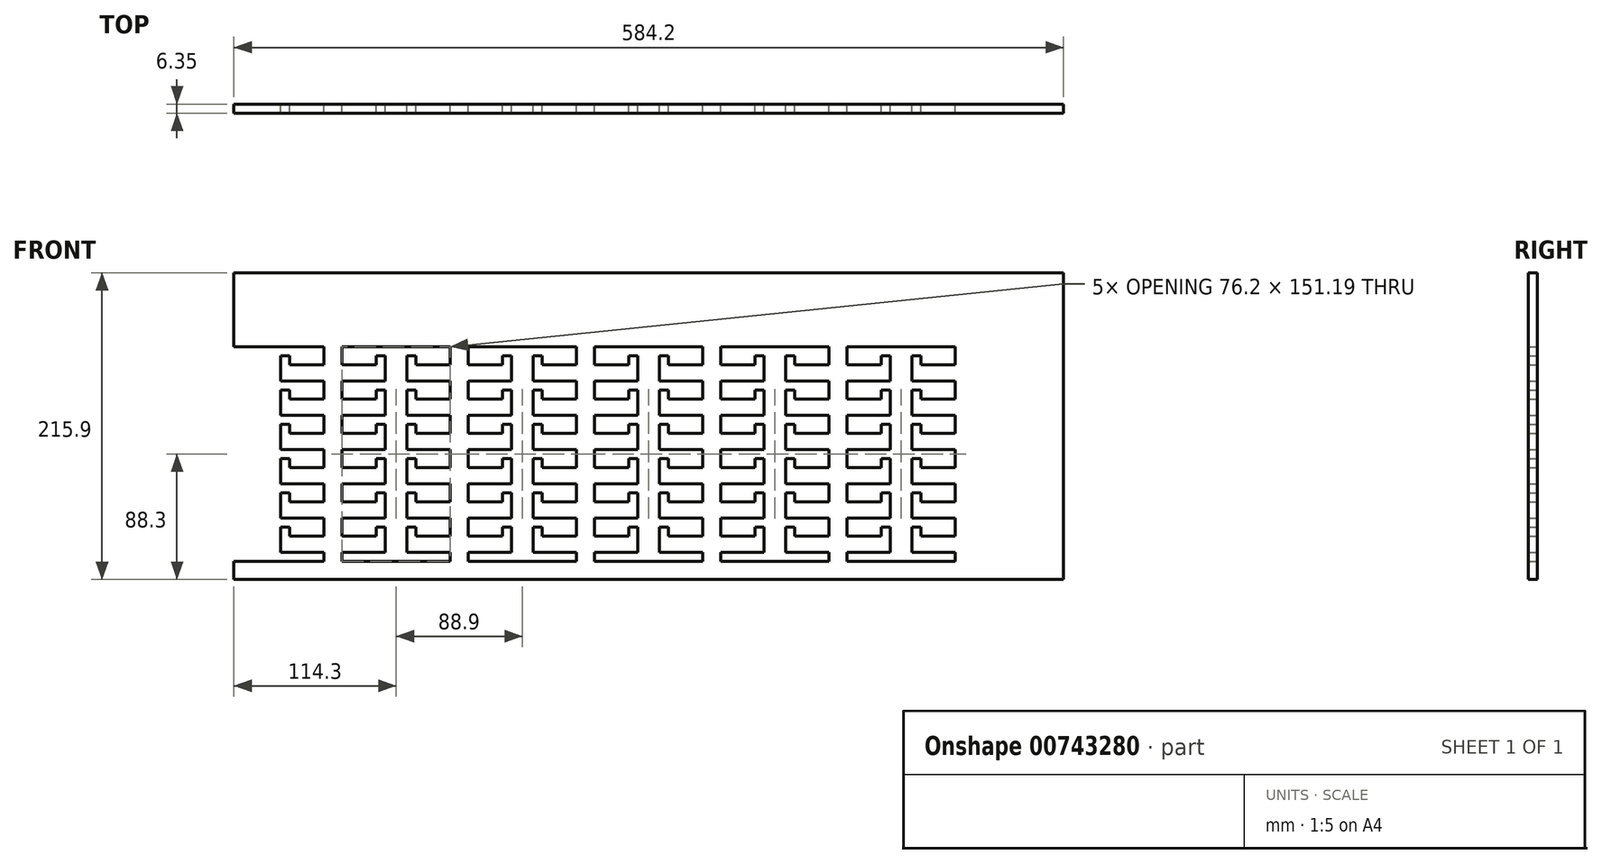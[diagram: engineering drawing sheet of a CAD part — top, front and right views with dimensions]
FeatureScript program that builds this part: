
annotation { "Feature Type Name" : "Feature", "Feature Type Description" : "" }
export const myFeature = defineFeature(function(context is Context, id is Id, definition is map)
    precondition{}
    {
        {
            var Q0;
            Q0=qCreatedBy(makeId("Front.planeOp"),FACE);
            var sketch = newSketch(context, id + "F0", { "sketchPlane" : qUnion([Q0])});
            skLineSegment(sketch, "E0", {"start": v(-97.96, -49.5) * mm, "end": v(-67.48, -49.5) * mm});
            skLineSegment(sketch, "E1", {"start": v(-67.48, -49.5) * mm, "end": v(-67.48, -31.72) * mm});
            skLineSegment(sketch, "E2", {"start": v(-67.48, -31.72) * mm, "end": v(-73.83, -31.72) * mm});
            skLineSegment(sketch, "E3", {"start": v(-73.83, -31.72) * mm, "end": v(-73.83, -38.07) * mm});
            skLineSegment(sketch, "E4", {"start": v(-73.83, -38.07) * mm, "end": v(-97.96, -38.07) * mm});
            skLineSegment(sketch, "E5", {"start": v(-97.96, -38.07) * mm, "end": v(-97.96, -25.37) * mm});
            skLineSegment(sketch, "E6", {"start": v(-97.96, -25.37) * mm, "end": v(-67.48, -25.37) * mm});
            skLineSegment(sketch, "E7", {"start": v(-67.48, -25.37) * mm, "end": v(-67.48, -7.6) * mm});
            skLineSegment(sketch, "E8", {"start": v(-67.48, -7.6) * mm, "end": v(-73.83, -7.6) * mm});
            skLineSegment(sketch, "E9", {"start": v(-73.83, -7.6) * mm, "end": v(-73.83, -13.94) * mm});
            skLineSegment(sketch, "E10", {"start": v(-73.83, -13.94) * mm, "end": v(-97.96, -13.94) * mm});
            skLineSegment(sketch, "E11", {"start": v(-97.96, -13.94) * mm, "end": v(-97.96, -1.24) * mm});
            skLineSegment(sketch, "E12", {"start": v(-97.96, -1.24) * mm, "end": v(-67.48, -1.24) * mm});
            skLineSegment(sketch, "E13", {"start": v(-67.48, -1.24) * mm, "end": v(-67.48, 16.54) * mm});
            skLineSegment(sketch, "E14", {"start": v(-67.48, 16.54) * mm, "end": v(-73.83, 16.54) * mm});
            skLineSegment(sketch, "E15", {"start": v(-73.83, 16.54) * mm, "end": v(-73.83, 10.19) * mm});
            skLineSegment(sketch, "E16", {"start": v(-73.83, 10.19) * mm, "end": v(-97.96, 10.19) * mm});
            skLineSegment(sketch, "E17", {"start": v(-97.96, 10.19) * mm, "end": v(-97.96, 22.89) * mm});
            skLineSegment(sketch, "E18", {"start": v(-97.96, 22.89) * mm, "end": v(-67.48, 22.89) * mm});
            skLineSegment(sketch, "E19", {"start": v(-67.48, 22.89) * mm, "end": v(-67.48, 40.67) * mm});
            skLineSegment(sketch, "E20", {"start": v(-67.48, 40.67) * mm, "end": v(-73.83, 40.67) * mm});
            skLineSegment(sketch, "E21", {"start": v(-73.83, 40.67) * mm, "end": v(-73.83, 34.32) * mm});
            skLineSegment(sketch, "E22", {"start": v(-73.83, 34.32) * mm, "end": v(-97.96, 34.32) * mm});
            skLineSegment(sketch, "E23", {"start": v(-97.96, 34.32) * mm, "end": v(-97.96, 47.02) * mm});
            skLineSegment(sketch, "E24", {"start": v(-97.96, 47.02) * mm, "end": v(-67.48, 47.02) * mm});
            skLineSegment(sketch, "E25", {"start": v(-67.48, 64.8) * mm, "end": v(-73.83, 64.8) * mm});
            skLineSegment(sketch, "E26", {"start": v(-73.83, 64.8) * mm, "end": v(-73.83, 58.45) * mm});
            skLineSegment(sketch, "E27", {"start": v(-73.83, 58.45) * mm, "end": v(-97.96, 58.45) * mm});
            skLineSegment(sketch, "E28", {"start": v(-97.96, 58.45) * mm, "end": v(-97.96, 71.15) * mm});
            skLineSegment(sketch, "E29", {"start": v(-21.76, -80.05) * mm, "end": v(-21.76, -73.63) * mm});
            skLineSegment(sketch, "E30", {"start": v(-21.76, -73.63) * mm, "end": v(-52.24, -73.63) * mm});
            skLineSegment(sketch, "E31", {"start": v(-52.24, -73.63) * mm, "end": v(-52.24, -55.85) * mm});
            skLineSegment(sketch, "E32", {"start": v(-52.24, -55.85) * mm, "end": v(-45.89, -55.85) * mm});
            skLineSegment(sketch, "E33", {"start": v(-45.89, -55.85) * mm, "end": v(-45.89, -62.2) * mm});
            skLineSegment(sketch, "E34", {"start": v(-45.89, -62.2) * mm, "end": v(-21.76, -62.2) * mm});
            skLineSegment(sketch, "E35", {"start": v(-21.76, -62.2) * mm, "end": v(-21.76, -49.5) * mm});
            skLineSegment(sketch, "E36", {"start": v(-21.76, -49.5) * mm, "end": v(-52.24, -49.5) * mm});
            skLineSegment(sketch, "E37", {"start": v(-52.24, -49.5) * mm, "end": v(-52.24, -31.72) * mm});
            skLineSegment(sketch, "E38", {"start": v(-52.24, -31.72) * mm, "end": v(-45.89, -31.72) * mm});
            skLineSegment(sketch, "E39", {"start": v(-45.89, -31.72) * mm, "end": v(-45.89, -38.07) * mm});
            skLineSegment(sketch, "E40", {"start": v(-45.89, -38.07) * mm, "end": v(-21.76, -38.07) * mm});
            skLineSegment(sketch, "E41", {"start": v(-21.76, -38.07) * mm, "end": v(-21.76, -25.37) * mm});
            skLineSegment(sketch, "E42", {"start": v(-21.76, -25.37) * mm, "end": v(-52.24, -25.37) * mm});
            skLineSegment(sketch, "E43", {"start": v(-52.24, -25.37) * mm, "end": v(-52.24, -7.6) * mm});
            skLineSegment(sketch, "E44", {"start": v(-52.24, -7.6) * mm, "end": v(-45.89, -7.6) * mm});
            skLineSegment(sketch, "E45", {"start": v(-45.89, -7.6) * mm, "end": v(-45.89, -13.94) * mm});
            skLineSegment(sketch, "E46", {"start": v(-45.89, -13.94) * mm, "end": v(-21.76, -13.94) * mm});
            skLineSegment(sketch, "E47", {"start": v(-21.76, -13.94) * mm, "end": v(-21.76, -1.24) * mm});
            skLineSegment(sketch, "E48", {"start": v(-21.76, -1.24) * mm, "end": v(-52.24, -1.24) * mm});
            skLineSegment(sketch, "E49", {"start": v(-52.24, -1.24) * mm, "end": v(-52.24, 16.54) * mm});
            skLineSegment(sketch, "E50", {"start": v(-52.24, 16.54) * mm, "end": v(-45.89, 16.54) * mm});
            skLineSegment(sketch, "E51", {"start": v(-45.89, 16.54) * mm, "end": v(-45.89, 10.19) * mm});
            skLineSegment(sketch, "E52", {"start": v(-45.89, 10.19) * mm, "end": v(-21.76, 10.19) * mm});
            skLineSegment(sketch, "E53", {"start": v(-21.76, 10.19) * mm, "end": v(-21.76, 22.89) * mm});
            skLineSegment(sketch, "E54", {"start": v(-21.76, 22.89) * mm, "end": v(-52.24, 22.89) * mm});
            skLineSegment(sketch, "E55", {"start": v(-52.24, 22.89) * mm, "end": v(-52.24, 40.67) * mm});
            skLineSegment(sketch, "E56", {"start": v(-52.24, 40.67) * mm, "end": v(-45.89, 40.67) * mm});
            skLineSegment(sketch, "E57", {"start": v(-45.89, 40.67) * mm, "end": v(-45.89, 34.32) * mm});
            skLineSegment(sketch, "E58", {"start": v(-45.89, 34.32) * mm, "end": v(-21.76, 34.32) * mm});
            skLineSegment(sketch, "E59", {"start": v(-21.76, 34.32) * mm, "end": v(-21.76, 47.02) * mm});
            skLineSegment(sketch, "E60", {"start": v(-21.76, 47.02) * mm, "end": v(-52.24, 47.02) * mm});
            skLineSegment(sketch, "E61", {"start": v(-52.24, 47.02) * mm, "end": v(-52.24, 64.8) * mm});
            skLineSegment(sketch, "E62", {"start": v(-52.24, 64.8) * mm, "end": v(-45.89, 64.8) * mm});
            skLineSegment(sketch, "E63", {"start": v(-45.89, 64.8) * mm, "end": v(-45.89, 58.45) * mm});
            skLineSegment(sketch, "E64", {"start": v(-45.89, 58.45) * mm, "end": v(-21.76, 58.45) * mm});
            skLineSegment(sketch, "E65", {"start": v(-21.76, 58.45) * mm, "end": v(-21.76, 71.15) * mm});
            skLineSegment(sketch, "E66", {"start": v(-67.48, 47.02) * mm, "end": v(-67.48, 64.8) * mm});
            skLineSegment(sketch, "E67", {"start": v(-67.48, -73.63) * mm, "end": v(-67.48, -55.85) * mm});
            skLineSegment(sketch, "E68", {"start": v(-73.83, -62.2) * mm, "end": v(-73.83, -55.85) * mm});
            skLineSegment(sketch, "E69", {"start": v(-73.83, -55.85) * mm, "end": v(-67.48, -55.85) * mm});
            skLineSegment(sketch, "E70", {"start": v(-67.48, -73.63) * mm, "end": v(-97.96, -73.63) * mm});
            skLineSegment(sketch, "E71", {"start": v(-97.96, -62.2) * mm, "end": v(-97.96, -49.5) * mm});
            skLineSegment(sketch, "E72", {"start": v(-97.96, -73.63) * mm, "end": v(-97.96, -80.05) * mm});
            skLineSegment(sketch, "E73", {"start": v(-97.96, -62.2) * mm, "end": v(-73.83, -62.2) * mm});
            skLineSegment(sketch, "E74", {"start": v(-97.96, -80.05) * mm, "end": v(-21.76, -80.05) * mm});
            skLineSegment(sketch, "E75", {"start": v(-97.96, 71.15) * mm, "end": v(-21.76, 71.15) * mm});
            skPoint(sketch, "E76", {"position": v(-59.86, 71.15) * mm});
            skPoint(sketch, "E77", {"position": v(-59.86, -80.05) * mm});
            skLineSegment(sketch, "E78", {"start": v(-186.86, -49.5) * mm, "end": v(-156.38, -49.5) * mm});
            skLineSegment(sketch, "E79", {"start": v(-156.38, -49.5) * mm, "end": v(-156.38, -31.72) * mm});
            skLineSegment(sketch, "E80", {"start": v(-156.38, -31.72) * mm, "end": v(-162.73, -31.72) * mm});
            skLineSegment(sketch, "E81", {"start": v(-162.73, -31.72) * mm, "end": v(-162.73, -38.07) * mm});
            skLineSegment(sketch, "E82", {"start": v(-162.73, -38.07) * mm, "end": v(-186.86, -38.07) * mm});
            skLineSegment(sketch, "E83", {"start": v(-186.86, -38.07) * mm, "end": v(-186.86, -25.37) * mm});
            skLineSegment(sketch, "E84", {"start": v(-186.86, -25.37) * mm, "end": v(-156.38, -25.37) * mm});
            skLineSegment(sketch, "E85", {"start": v(-156.38, -25.37) * mm, "end": v(-156.38, -7.6) * mm});
            skLineSegment(sketch, "E86", {"start": v(-156.38, -7.6) * mm, "end": v(-162.73, -7.6) * mm});
            skLineSegment(sketch, "E87", {"start": v(-162.73, -7.6) * mm, "end": v(-162.73, -13.94) * mm});
            skLineSegment(sketch, "E88", {"start": v(-162.73, -13.94) * mm, "end": v(-186.86, -13.94) * mm});
            skLineSegment(sketch, "E89", {"start": v(-186.86, -13.94) * mm, "end": v(-186.86, -1.24) * mm});
            skLineSegment(sketch, "E90", {"start": v(-186.86, -1.24) * mm, "end": v(-156.38, -1.24) * mm});
            skLineSegment(sketch, "E91", {"start": v(-156.38, -1.24) * mm, "end": v(-156.38, 16.54) * mm});
            skLineSegment(sketch, "E92", {"start": v(-156.38, 16.54) * mm, "end": v(-162.73, 16.54) * mm});
            skLineSegment(sketch, "E93", {"start": v(-162.73, 16.54) * mm, "end": v(-162.73, 10.19) * mm});
            skLineSegment(sketch, "E94", {"start": v(-162.73, 10.19) * mm, "end": v(-186.86, 10.19) * mm});
            skLineSegment(sketch, "E95", {"start": v(-186.86, 10.19) * mm, "end": v(-186.86, 22.89) * mm});
            skLineSegment(sketch, "E96", {"start": v(-186.86, 22.89) * mm, "end": v(-156.38, 22.89) * mm});
            skLineSegment(sketch, "E97", {"start": v(-156.38, 22.89) * mm, "end": v(-156.38, 40.67) * mm});
            skLineSegment(sketch, "E98", {"start": v(-156.38, 40.67) * mm, "end": v(-162.73, 40.67) * mm});
            skLineSegment(sketch, "E99", {"start": v(-162.73, 40.67) * mm, "end": v(-162.73, 34.32) * mm});
            skLineSegment(sketch, "E100", {"start": v(-162.73, 34.32) * mm, "end": v(-186.86, 34.32) * mm});
            skLineSegment(sketch, "E101", {"start": v(-186.86, 34.32) * mm, "end": v(-186.86, 47.02) * mm});
            skLineSegment(sketch, "E102", {"start": v(-186.86, 47.02) * mm, "end": v(-156.38, 47.02) * mm});
            skLineSegment(sketch, "E103", {"start": v(-156.38, 64.8) * mm, "end": v(-162.73, 64.8) * mm});
            skLineSegment(sketch, "E104", {"start": v(-162.73, 64.8) * mm, "end": v(-162.73, 58.45) * mm});
            skLineSegment(sketch, "E105", {"start": v(-162.73, 58.45) * mm, "end": v(-186.86, 58.45) * mm});
            skLineSegment(sketch, "E106", {"start": v(-186.86, 58.45) * mm, "end": v(-186.86, 71.15) * mm});
            skLineSegment(sketch, "E107", {"start": v(-110.66, -80.05) * mm, "end": v(-110.66, -73.63) * mm});
            skLineSegment(sketch, "E108", {"start": v(-110.66, -73.63) * mm, "end": v(-141.14, -73.63) * mm});
            skLineSegment(sketch, "E109", {"start": v(-141.14, -73.63) * mm, "end": v(-141.14, -55.85) * mm});
            skLineSegment(sketch, "E110", {"start": v(-141.14, -55.85) * mm, "end": v(-134.79, -55.85) * mm});
            skLineSegment(sketch, "E111", {"start": v(-134.79, -55.85) * mm, "end": v(-134.79, -62.2) * mm});
            skLineSegment(sketch, "E112", {"start": v(-134.79, -62.2) * mm, "end": v(-110.66, -62.2) * mm});
            skLineSegment(sketch, "E113", {"start": v(-110.66, -62.2) * mm, "end": v(-110.66, -49.5) * mm});
            skLineSegment(sketch, "E114", {"start": v(-110.66, -49.5) * mm, "end": v(-141.14, -49.5) * mm});
            skLineSegment(sketch, "E115", {"start": v(-141.14, -49.5) * mm, "end": v(-141.14, -31.72) * mm});
            skLineSegment(sketch, "E116", {"start": v(-141.14, -31.72) * mm, "end": v(-134.79, -31.72) * mm});
            skLineSegment(sketch, "E117", {"start": v(-134.79, -31.72) * mm, "end": v(-134.79, -38.07) * mm});
            skLineSegment(sketch, "E118", {"start": v(-134.79, -38.07) * mm, "end": v(-110.66, -38.07) * mm});
            skLineSegment(sketch, "E119", {"start": v(-110.66, -38.07) * mm, "end": v(-110.66, -25.37) * mm});
            skLineSegment(sketch, "E120", {"start": v(-110.66, -25.37) * mm, "end": v(-141.14, -25.37) * mm});
            skLineSegment(sketch, "E121", {"start": v(-141.14, -25.37) * mm, "end": v(-141.14, -7.6) * mm});
            skLineSegment(sketch, "E122", {"start": v(-141.14, -7.6) * mm, "end": v(-134.79, -7.6) * mm});
            skLineSegment(sketch, "E123", {"start": v(-134.79, -7.6) * mm, "end": v(-134.79, -13.94) * mm});
            skLineSegment(sketch, "E124", {"start": v(-134.79, -13.94) * mm, "end": v(-110.66, -13.94) * mm});
            skLineSegment(sketch, "E125", {"start": v(-110.66, -13.94) * mm, "end": v(-110.66, -1.24) * mm});
            skLineSegment(sketch, "E126", {"start": v(-110.66, -1.24) * mm, "end": v(-141.14, -1.24) * mm});
            skLineSegment(sketch, "E127", {"start": v(-141.14, -1.24) * mm, "end": v(-141.14, 16.54) * mm});
            skLineSegment(sketch, "E128", {"start": v(-141.14, 16.54) * mm, "end": v(-134.79, 16.54) * mm});
            skLineSegment(sketch, "E129", {"start": v(-134.79, 16.54) * mm, "end": v(-134.79, 10.19) * mm});
            skLineSegment(sketch, "E130", {"start": v(-134.79, 10.19) * mm, "end": v(-110.66, 10.19) * mm});
            skLineSegment(sketch, "E131", {"start": v(-110.66, 10.19) * mm, "end": v(-110.66, 22.89) * mm});
            skLineSegment(sketch, "E132", {"start": v(-110.66, 22.89) * mm, "end": v(-141.14, 22.89) * mm});
            skLineSegment(sketch, "E133", {"start": v(-141.14, 22.89) * mm, "end": v(-141.14, 40.67) * mm});
            skLineSegment(sketch, "E134", {"start": v(-141.14, 40.67) * mm, "end": v(-134.79, 40.67) * mm});
            skLineSegment(sketch, "E135", {"start": v(-134.79, 40.67) * mm, "end": v(-134.79, 34.32) * mm});
            skLineSegment(sketch, "E136", {"start": v(-134.79, 34.32) * mm, "end": v(-110.66, 34.32) * mm});
            skLineSegment(sketch, "E137", {"start": v(-110.66, 34.32) * mm, "end": v(-110.66, 47.02) * mm});
            skLineSegment(sketch, "E138", {"start": v(-110.66, 47.02) * mm, "end": v(-141.14, 47.02) * mm});
            skLineSegment(sketch, "E139", {"start": v(-141.14, 47.02) * mm, "end": v(-141.14, 64.8) * mm});
            skLineSegment(sketch, "E140", {"start": v(-141.14, 64.8) * mm, "end": v(-134.79, 64.8) * mm});
            skLineSegment(sketch, "E141", {"start": v(-134.79, 64.8) * mm, "end": v(-134.79, 58.45) * mm});
            skLineSegment(sketch, "E142", {"start": v(-134.79, 58.45) * mm, "end": v(-110.66, 58.45) * mm});
            skLineSegment(sketch, "E143", {"start": v(-110.66, 58.45) * mm, "end": v(-110.66, 71.15) * mm});
            skLineSegment(sketch, "E144", {"start": v(-156.38, 47.02) * mm, "end": v(-156.38, 64.8) * mm});
            skLineSegment(sketch, "E145", {"start": v(-156.38, -73.63) * mm, "end": v(-156.38, -55.85) * mm});
            skLineSegment(sketch, "E146", {"start": v(-162.73, -62.2) * mm, "end": v(-162.73, -55.85) * mm});
            skLineSegment(sketch, "E147", {"start": v(-162.73, -55.85) * mm, "end": v(-156.38, -55.85) * mm});
            skLineSegment(sketch, "E148", {"start": v(-156.38, -73.63) * mm, "end": v(-186.86, -73.63) * mm});
            skLineSegment(sketch, "E149", {"start": v(-186.86, -62.2) * mm, "end": v(-186.86, -49.5) * mm});
            skLineSegment(sketch, "E150", {"start": v(-186.86, -73.63) * mm, "end": v(-186.86, -80.05) * mm});
            skLineSegment(sketch, "E151", {"start": v(-186.86, -62.2) * mm, "end": v(-162.73, -62.2) * mm});
            skLineSegment(sketch, "E152", {"start": v(-186.86, -80.05) * mm, "end": v(-110.66, -80.05) * mm});
            skLineSegment(sketch, "E153", {"start": v(-186.86, 71.15) * mm, "end": v(-110.66, 71.15) * mm});
            skPoint(sketch, "E154", {"position": v(-148.76, 71.15) * mm});
            skPoint(sketch, "E155", {"position": v(-148.76, -80.05) * mm});
            skLineSegment(sketch, "E156", {"start": v(-275.76, -49.5) * mm, "end": v(-245.28, -49.5) * mm});
            skLineSegment(sketch, "E157", {"start": v(-245.28, -49.5) * mm, "end": v(-245.28, -31.72) * mm});
            skLineSegment(sketch, "E158", {"start": v(-245.28, -31.72) * mm, "end": v(-251.63, -31.72) * mm});
            skLineSegment(sketch, "E159", {"start": v(-251.63, -31.72) * mm, "end": v(-251.63, -38.07) * mm});
            skLineSegment(sketch, "E160", {"start": v(-251.63, -38.07) * mm, "end": v(-275.76, -38.07) * mm});
            skLineSegment(sketch, "E161", {"start": v(-275.76, -38.07) * mm, "end": v(-275.76, -25.37) * mm});
            skLineSegment(sketch, "E162", {"start": v(-275.76, -25.37) * mm, "end": v(-245.28, -25.37) * mm});
            skLineSegment(sketch, "E163", {"start": v(-245.28, -25.37) * mm, "end": v(-245.28, -7.6) * mm});
            skLineSegment(sketch, "E164", {"start": v(-245.28, -7.6) * mm, "end": v(-251.63, -7.6) * mm});
            skLineSegment(sketch, "E165", {"start": v(-251.63, -7.6) * mm, "end": v(-251.63, -13.94) * mm});
            skLineSegment(sketch, "E166", {"start": v(-251.63, -13.94) * mm, "end": v(-275.76, -13.94) * mm});
            skLineSegment(sketch, "E167", {"start": v(-275.76, -13.94) * mm, "end": v(-275.76, -1.24) * mm});
            skLineSegment(sketch, "E168", {"start": v(-275.76, -1.24) * mm, "end": v(-245.28, -1.24) * mm});
            skLineSegment(sketch, "E169", {"start": v(-245.28, -1.24) * mm, "end": v(-245.28, 16.54) * mm});
            skLineSegment(sketch, "E170", {"start": v(-245.28, 16.54) * mm, "end": v(-251.63, 16.54) * mm});
            skLineSegment(sketch, "E171", {"start": v(-251.63, 16.54) * mm, "end": v(-251.63, 10.19) * mm});
            skLineSegment(sketch, "E172", {"start": v(-251.63, 10.19) * mm, "end": v(-275.76, 10.19) * mm});
            skLineSegment(sketch, "E173", {"start": v(-275.76, 10.19) * mm, "end": v(-275.76, 22.89) * mm});
            skLineSegment(sketch, "E174", {"start": v(-275.76, 22.89) * mm, "end": v(-245.28, 22.89) * mm});
            skLineSegment(sketch, "E175", {"start": v(-245.28, 22.89) * mm, "end": v(-245.28, 40.67) * mm});
            skLineSegment(sketch, "E176", {"start": v(-245.28, 40.67) * mm, "end": v(-251.63, 40.67) * mm});
            skLineSegment(sketch, "E177", {"start": v(-251.63, 40.67) * mm, "end": v(-251.63, 34.32) * mm});
            skLineSegment(sketch, "E178", {"start": v(-251.63, 34.32) * mm, "end": v(-275.76, 34.32) * mm});
            skLineSegment(sketch, "E179", {"start": v(-275.76, 34.32) * mm, "end": v(-275.76, 47.02) * mm});
            skLineSegment(sketch, "E180", {"start": v(-275.76, 47.02) * mm, "end": v(-245.28, 47.02) * mm});
            skLineSegment(sketch, "E181", {"start": v(-245.28, 64.8) * mm, "end": v(-251.63, 64.8) * mm});
            skLineSegment(sketch, "E182", {"start": v(-251.63, 64.8) * mm, "end": v(-251.63, 58.45) * mm});
            skLineSegment(sketch, "E183", {"start": v(-251.63, 58.45) * mm, "end": v(-275.76, 58.45) * mm});
            skLineSegment(sketch, "E184", {"start": v(-275.76, 58.45) * mm, "end": v(-275.76, 71.15) * mm});
            skLineSegment(sketch, "E185", {"start": v(-199.56, -80.05) * mm, "end": v(-199.56, -73.63) * mm});
            skLineSegment(sketch, "E186", {"start": v(-199.56, -73.63) * mm, "end": v(-230.04, -73.63) * mm});
            skLineSegment(sketch, "E187", {"start": v(-230.04, -73.63) * mm, "end": v(-230.04, -55.85) * mm});
            skLineSegment(sketch, "E188", {"start": v(-230.04, -55.85) * mm, "end": v(-223.69, -55.85) * mm});
            skLineSegment(sketch, "E189", {"start": v(-223.69, -55.85) * mm, "end": v(-223.69, -62.2) * mm});
            skLineSegment(sketch, "E190", {"start": v(-223.69, -62.2) * mm, "end": v(-199.56, -62.2) * mm});
            skLineSegment(sketch, "E191", {"start": v(-199.56, -62.2) * mm, "end": v(-199.56, -49.5) * mm});
            skLineSegment(sketch, "E192", {"start": v(-199.56, -49.5) * mm, "end": v(-230.04, -49.5) * mm});
            skLineSegment(sketch, "E193", {"start": v(-230.04, -49.5) * mm, "end": v(-230.04, -31.72) * mm});
            skLineSegment(sketch, "E194", {"start": v(-230.04, -31.72) * mm, "end": v(-223.69, -31.72) * mm});
            skLineSegment(sketch, "E195", {"start": v(-223.69, -31.72) * mm, "end": v(-223.69, -38.07) * mm});
            skLineSegment(sketch, "E196", {"start": v(-223.69, -38.07) * mm, "end": v(-199.56, -38.07) * mm});
            skLineSegment(sketch, "E197", {"start": v(-199.56, -38.07) * mm, "end": v(-199.56, -25.37) * mm});
            skLineSegment(sketch, "E198", {"start": v(-199.56, -25.37) * mm, "end": v(-230.04, -25.37) * mm});
            skLineSegment(sketch, "E199", {"start": v(-230.04, -25.37) * mm, "end": v(-230.04, -7.6) * mm});
            skLineSegment(sketch, "E200", {"start": v(-230.04, -7.6) * mm, "end": v(-223.69, -7.6) * mm});
            skLineSegment(sketch, "E201", {"start": v(-223.69, -7.6) * mm, "end": v(-223.69, -13.94) * mm});
            skLineSegment(sketch, "E202", {"start": v(-223.69, -13.94) * mm, "end": v(-199.56, -13.94) * mm});
            skLineSegment(sketch, "E203", {"start": v(-199.56, -13.94) * mm, "end": v(-199.56, -1.24) * mm});
            skLineSegment(sketch, "E204", {"start": v(-199.56, -1.24) * mm, "end": v(-230.04, -1.24) * mm});
            skLineSegment(sketch, "E205", {"start": v(-230.04, -1.24) * mm, "end": v(-230.04, 16.54) * mm});
            skLineSegment(sketch, "E206", {"start": v(-230.04, 16.54) * mm, "end": v(-223.69, 16.54) * mm});
            skLineSegment(sketch, "E207", {"start": v(-223.69, 16.54) * mm, "end": v(-223.69, 10.19) * mm});
            skLineSegment(sketch, "E208", {"start": v(-223.69, 10.19) * mm, "end": v(-199.56, 10.19) * mm});
            skLineSegment(sketch, "E209", {"start": v(-199.56, 10.19) * mm, "end": v(-199.56, 22.89) * mm});
            skLineSegment(sketch, "E210", {"start": v(-199.56, 22.89) * mm, "end": v(-230.04, 22.89) * mm});
            skLineSegment(sketch, "E211", {"start": v(-230.04, 22.89) * mm, "end": v(-230.04, 40.67) * mm});
            skLineSegment(sketch, "E212", {"start": v(-230.04, 40.67) * mm, "end": v(-223.69, 40.67) * mm});
            skLineSegment(sketch, "E213", {"start": v(-223.69, 40.67) * mm, "end": v(-223.69, 34.32) * mm});
            skLineSegment(sketch, "E214", {"start": v(-223.69, 34.32) * mm, "end": v(-199.56, 34.32) * mm});
            skLineSegment(sketch, "E215", {"start": v(-199.56, 34.32) * mm, "end": v(-199.56, 47.02) * mm});
            skLineSegment(sketch, "E216", {"start": v(-199.56, 47.02) * mm, "end": v(-230.04, 47.02) * mm});
            skLineSegment(sketch, "E217", {"start": v(-230.04, 47.02) * mm, "end": v(-230.04, 64.8) * mm});
            skLineSegment(sketch, "E218", {"start": v(-230.04, 64.8) * mm, "end": v(-223.69, 64.8) * mm});
            skLineSegment(sketch, "E219", {"start": v(-223.69, 64.8) * mm, "end": v(-223.69, 58.45) * mm});
            skLineSegment(sketch, "E220", {"start": v(-223.69, 58.45) * mm, "end": v(-199.56, 58.45) * mm});
            skLineSegment(sketch, "E221", {"start": v(-199.56, 58.45) * mm, "end": v(-199.56, 71.15) * mm});
            skLineSegment(sketch, "E222", {"start": v(-245.28, 47.02) * mm, "end": v(-245.28, 64.8) * mm});
            skLineSegment(sketch, "E223", {"start": v(-245.28, -73.63) * mm, "end": v(-245.28, -55.85) * mm});
            skLineSegment(sketch, "E224", {"start": v(-251.63, -62.2) * mm, "end": v(-251.63, -55.85) * mm});
            skLineSegment(sketch, "E225", {"start": v(-251.63, -55.85) * mm, "end": v(-245.28, -55.85) * mm});
            skLineSegment(sketch, "E226", {"start": v(-245.28, -73.63) * mm, "end": v(-275.76, -73.63) * mm});
            skLineSegment(sketch, "E227", {"start": v(-275.76, -62.2) * mm, "end": v(-275.76, -49.5) * mm});
            skLineSegment(sketch, "E228", {"start": v(-275.76, -73.63) * mm, "end": v(-275.76, -80.05) * mm});
            skLineSegment(sketch, "E229", {"start": v(-275.76, -62.2) * mm, "end": v(-251.63, -62.2) * mm});
            skLineSegment(sketch, "E230", {"start": v(-275.76, -80.05) * mm, "end": v(-199.56, -80.05) * mm});
            skLineSegment(sketch, "E231", {"start": v(-275.76, 71.15) * mm, "end": v(-199.56, 71.15) * mm});
            skPoint(sketch, "E232", {"position": v(-237.66, 71.15) * mm});
            skPoint(sketch, "E233", {"position": v(-237.66, -80.05) * mm});
            skLineSegment(sketch, "E234", {"start": v(-364.66, -49.5) * mm, "end": v(-334.18, -49.5) * mm});
            skLineSegment(sketch, "E235", {"start": v(-334.18, -49.5) * mm, "end": v(-334.18, -31.72) * mm});
            skLineSegment(sketch, "E236", {"start": v(-334.18, -31.72) * mm, "end": v(-340.53, -31.72) * mm});
            skLineSegment(sketch, "E237", {"start": v(-340.53, -31.72) * mm, "end": v(-340.53, -38.07) * mm});
            skLineSegment(sketch, "E238", {"start": v(-340.53, -38.07) * mm, "end": v(-364.66, -38.07) * mm});
            skLineSegment(sketch, "E239", {"start": v(-364.66, -38.07) * mm, "end": v(-364.66, -25.37) * mm});
            skLineSegment(sketch, "E240", {"start": v(-364.66, -25.37) * mm, "end": v(-334.18, -25.37) * mm});
            skLineSegment(sketch, "E241", {"start": v(-334.18, -25.37) * mm, "end": v(-334.18, -7.6) * mm});
            skLineSegment(sketch, "E242", {"start": v(-334.18, -7.6) * mm, "end": v(-340.53, -7.6) * mm});
            skLineSegment(sketch, "E243", {"start": v(-340.53, -7.6) * mm, "end": v(-340.53, -13.94) * mm});
            skLineSegment(sketch, "E244", {"start": v(-340.53, -13.94) * mm, "end": v(-364.66, -13.94) * mm});
            skLineSegment(sketch, "E245", {"start": v(-364.66, -13.94) * mm, "end": v(-364.66, -1.24) * mm});
            skLineSegment(sketch, "E246", {"start": v(-364.66, -1.24) * mm, "end": v(-334.18, -1.24) * mm});
            skLineSegment(sketch, "E247", {"start": v(-334.18, -1.24) * mm, "end": v(-334.18, 16.54) * mm});
            skLineSegment(sketch, "E248", {"start": v(-334.18, 16.54) * mm, "end": v(-340.53, 16.54) * mm});
            skLineSegment(sketch, "E249", {"start": v(-340.53, 16.54) * mm, "end": v(-340.53, 10.19) * mm});
            skLineSegment(sketch, "E250", {"start": v(-340.53, 10.19) * mm, "end": v(-364.66, 10.19) * mm});
            skLineSegment(sketch, "E251", {"start": v(-364.66, 10.19) * mm, "end": v(-364.66, 22.89) * mm});
            skLineSegment(sketch, "E252", {"start": v(-364.66, 22.89) * mm, "end": v(-334.18, 22.89) * mm});
            skLineSegment(sketch, "E253", {"start": v(-334.18, 22.89) * mm, "end": v(-334.18, 40.67) * mm});
            skLineSegment(sketch, "E254", {"start": v(-334.18, 40.67) * mm, "end": v(-340.53, 40.67) * mm});
            skLineSegment(sketch, "E255", {"start": v(-340.53, 40.67) * mm, "end": v(-340.53, 34.32) * mm});
            skLineSegment(sketch, "E256", {"start": v(-340.53, 34.32) * mm, "end": v(-364.66, 34.32) * mm});
            skLineSegment(sketch, "E257", {"start": v(-364.66, 34.32) * mm, "end": v(-364.66, 47.02) * mm});
            skLineSegment(sketch, "E258", {"start": v(-364.66, 47.02) * mm, "end": v(-334.18, 47.02) * mm});
            skLineSegment(sketch, "E259", {"start": v(-334.18, 64.8) * mm, "end": v(-340.53, 64.8) * mm});
            skLineSegment(sketch, "E260", {"start": v(-340.53, 64.8) * mm, "end": v(-340.53, 58.45) * mm});
            skLineSegment(sketch, "E261", {"start": v(-340.53, 58.45) * mm, "end": v(-364.66, 58.45) * mm});
            skLineSegment(sketch, "E262", {"start": v(-364.66, 58.45) * mm, "end": v(-364.66, 71.15) * mm});
            skLineSegment(sketch, "E263", {"start": v(-288.46, -80.05) * mm, "end": v(-288.46, -73.63) * mm});
            skLineSegment(sketch, "E264", {"start": v(-288.46, -73.63) * mm, "end": v(-318.94, -73.63) * mm});
            skLineSegment(sketch, "E265", {"start": v(-318.94, -73.63) * mm, "end": v(-318.94, -55.85) * mm});
            skLineSegment(sketch, "E266", {"start": v(-318.94, -55.85) * mm, "end": v(-312.59, -55.85) * mm});
            skLineSegment(sketch, "E267", {"start": v(-312.59, -55.85) * mm, "end": v(-312.59, -62.2) * mm});
            skLineSegment(sketch, "E268", {"start": v(-312.59, -62.2) * mm, "end": v(-288.46, -62.2) * mm});
            skLineSegment(sketch, "E269", {"start": v(-288.46, -62.2) * mm, "end": v(-288.46, -49.5) * mm});
            skLineSegment(sketch, "E270", {"start": v(-288.46, -49.5) * mm, "end": v(-318.94, -49.5) * mm});
            skLineSegment(sketch, "E271", {"start": v(-318.94, -49.5) * mm, "end": v(-318.94, -31.72) * mm});
            skLineSegment(sketch, "E272", {"start": v(-318.94, -31.72) * mm, "end": v(-312.59, -31.72) * mm});
            skLineSegment(sketch, "E273", {"start": v(-312.59, -31.72) * mm, "end": v(-312.59, -38.07) * mm});
            skLineSegment(sketch, "E274", {"start": v(-312.59, -38.07) * mm, "end": v(-288.46, -38.07) * mm});
            skLineSegment(sketch, "E275", {"start": v(-288.46, -38.07) * mm, "end": v(-288.46, -25.37) * mm});
            skLineSegment(sketch, "E276", {"start": v(-288.46, -25.37) * mm, "end": v(-318.94, -25.37) * mm});
            skLineSegment(sketch, "E277", {"start": v(-318.94, -25.37) * mm, "end": v(-318.94, -7.6) * mm});
            skLineSegment(sketch, "E278", {"start": v(-318.94, -7.6) * mm, "end": v(-312.59, -7.6) * mm});
            skLineSegment(sketch, "E279", {"start": v(-312.59, -7.6) * mm, "end": v(-312.59, -13.94) * mm});
            skLineSegment(sketch, "E280", {"start": v(-312.59, -13.94) * mm, "end": v(-288.46, -13.94) * mm});
            skLineSegment(sketch, "E281", {"start": v(-288.46, -13.94) * mm, "end": v(-288.46, -1.24) * mm});
            skLineSegment(sketch, "E282", {"start": v(-288.46, -1.24) * mm, "end": v(-318.94, -1.24) * mm});
            skLineSegment(sketch, "E283", {"start": v(-318.94, -1.24) * mm, "end": v(-318.94, 16.54) * mm});
            skLineSegment(sketch, "E284", {"start": v(-318.94, 16.54) * mm, "end": v(-312.59, 16.54) * mm});
            skLineSegment(sketch, "E285", {"start": v(-312.59, 16.54) * mm, "end": v(-312.59, 10.19) * mm});
            skLineSegment(sketch, "E286", {"start": v(-312.59, 10.19) * mm, "end": v(-288.46, 10.19) * mm});
            skLineSegment(sketch, "E287", {"start": v(-288.46, 10.19) * mm, "end": v(-288.46, 22.89) * mm});
            skLineSegment(sketch, "E288", {"start": v(-288.46, 22.89) * mm, "end": v(-318.94, 22.89) * mm});
            skLineSegment(sketch, "E289", {"start": v(-318.94, 22.89) * mm, "end": v(-318.94, 40.67) * mm});
            skLineSegment(sketch, "E290", {"start": v(-318.94, 40.67) * mm, "end": v(-312.59, 40.67) * mm});
            skLineSegment(sketch, "E291", {"start": v(-312.59, 40.67) * mm, "end": v(-312.59, 34.32) * mm});
            skLineSegment(sketch, "E292", {"start": v(-312.59, 34.32) * mm, "end": v(-288.46, 34.32) * mm});
            skLineSegment(sketch, "E293", {"start": v(-288.46, 34.32) * mm, "end": v(-288.46, 47.02) * mm});
            skLineSegment(sketch, "E294", {"start": v(-288.46, 47.02) * mm, "end": v(-318.94, 47.02) * mm});
            skLineSegment(sketch, "E295", {"start": v(-318.94, 47.02) * mm, "end": v(-318.94, 64.8) * mm});
            skLineSegment(sketch, "E296", {"start": v(-318.94, 64.8) * mm, "end": v(-312.59, 64.8) * mm});
            skLineSegment(sketch, "E297", {"start": v(-312.59, 64.8) * mm, "end": v(-312.59, 58.45) * mm});
            skLineSegment(sketch, "E298", {"start": v(-312.59, 58.45) * mm, "end": v(-288.46, 58.45) * mm});
            skLineSegment(sketch, "E299", {"start": v(-288.46, 58.45) * mm, "end": v(-288.46, 71.15) * mm});
            skLineSegment(sketch, "E300", {"start": v(-334.18, 47.02) * mm, "end": v(-334.18, 64.8) * mm});
            skLineSegment(sketch, "E301", {"start": v(-334.18, -73.63) * mm, "end": v(-334.18, -55.85) * mm});
            skLineSegment(sketch, "E302", {"start": v(-340.53, -62.2) * mm, "end": v(-340.53, -55.85) * mm});
            skLineSegment(sketch, "E303", {"start": v(-340.53, -55.85) * mm, "end": v(-334.18, -55.85) * mm});
            skLineSegment(sketch, "E304", {"start": v(-334.18, -73.63) * mm, "end": v(-364.66, -73.63) * mm});
            skLineSegment(sketch, "E305", {"start": v(-364.66, -62.2) * mm, "end": v(-364.66, -49.5) * mm});
            skLineSegment(sketch, "E306", {"start": v(-364.66, -73.63) * mm, "end": v(-364.66, -80.05) * mm});
            skLineSegment(sketch, "E307", {"start": v(-364.66, -62.2) * mm, "end": v(-340.53, -62.2) * mm});
            skLineSegment(sketch, "E308", {"start": v(-364.66, -80.05) * mm, "end": v(-288.46, -80.05) * mm});
            skLineSegment(sketch, "E309", {"start": v(-364.66, 71.15) * mm, "end": v(-288.46, 71.15) * mm});
            skPoint(sketch, "E310", {"position": v(-326.56, 71.15) * mm});
            skPoint(sketch, "E311", {"position": v(-326.56, -80.05) * mm});
            skLineSegment(sketch, "E312.bottom", {"start": v(54.44, 123.15) * mm, "end": v(-529.76, 123.15) * mm});
            skLineSegment(sketch, "E312.top", {"start": v(54.44, -92.75) * mm, "end": v(-529.76, -92.75) * mm});
            skLineSegment(sketch, "E312.left", {"start": v(54.44, 123.15) * mm, "end": v(54.44, -92.75) * mm});
            skLineSegment(sketch, "E312.right", {"start": v(-529.76, 123.15) * mm, "end": v(-529.76, -92.75) * mm});
            skPoint(sketch, "E313", {"position": v(-237.66, 123.15) * mm});
            skLineSegment(sketch, "E314", {"start": v(-453.56, -49.5) * mm, "end": v(-423.08, -49.5) * mm});
            skLineSegment(sketch, "E315", {"start": v(-423.08, -49.5) * mm, "end": v(-423.08, -31.72) * mm});
            skLineSegment(sketch, "E316", {"start": v(-423.08, -31.72) * mm, "end": v(-429.43, -31.72) * mm});
            skLineSegment(sketch, "E317", {"start": v(-429.43, -31.72) * mm, "end": v(-429.43, -38.07) * mm});
            skLineSegment(sketch, "E318", {"start": v(-429.43, -38.07) * mm, "end": v(-453.56, -38.07) * mm});
            skLineSegment(sketch, "E319", {"start": v(-453.56, -38.07) * mm, "end": v(-453.56, -25.37) * mm});
            skLineSegment(sketch, "E320", {"start": v(-453.56, -25.37) * mm, "end": v(-423.08, -25.37) * mm});
            skLineSegment(sketch, "E321", {"start": v(-423.08, -25.37) * mm, "end": v(-423.08, -7.6) * mm});
            skLineSegment(sketch, "E322", {"start": v(-423.08, -7.6) * mm, "end": v(-429.43, -7.6) * mm});
            skLineSegment(sketch, "E323", {"start": v(-429.43, -7.6) * mm, "end": v(-429.43, -13.94) * mm});
            skLineSegment(sketch, "E324", {"start": v(-429.43, -13.94) * mm, "end": v(-453.56, -13.94) * mm});
            skLineSegment(sketch, "E325", {"start": v(-453.56, -13.94) * mm, "end": v(-453.56, -1.24) * mm});
            skLineSegment(sketch, "E326", {"start": v(-453.56, -1.24) * mm, "end": v(-423.08, -1.24) * mm});
            skLineSegment(sketch, "E327", {"start": v(-423.08, -1.24) * mm, "end": v(-423.08, 16.54) * mm});
            skLineSegment(sketch, "E328", {"start": v(-423.08, 16.54) * mm, "end": v(-429.43, 16.54) * mm});
            skLineSegment(sketch, "E329", {"start": v(-429.43, 16.54) * mm, "end": v(-429.43, 10.19) * mm});
            skLineSegment(sketch, "E330", {"start": v(-429.43, 10.19) * mm, "end": v(-453.56, 10.19) * mm});
            skLineSegment(sketch, "E331", {"start": v(-453.56, 10.19) * mm, "end": v(-453.56, 22.89) * mm});
            skLineSegment(sketch, "E332", {"start": v(-453.56, 22.89) * mm, "end": v(-423.08, 22.89) * mm});
            skLineSegment(sketch, "E333", {"start": v(-423.08, 22.89) * mm, "end": v(-423.08, 40.67) * mm});
            skLineSegment(sketch, "E334", {"start": v(-423.08, 40.67) * mm, "end": v(-429.43, 40.67) * mm});
            skLineSegment(sketch, "E335", {"start": v(-429.43, 40.67) * mm, "end": v(-429.43, 34.32) * mm});
            skLineSegment(sketch, "E336", {"start": v(-429.43, 34.32) * mm, "end": v(-453.56, 34.32) * mm});
            skLineSegment(sketch, "E337", {"start": v(-453.56, 34.32) * mm, "end": v(-453.56, 47.02) * mm});
            skLineSegment(sketch, "E338", {"start": v(-453.56, 47.02) * mm, "end": v(-423.08, 47.02) * mm});
            skLineSegment(sketch, "E339", {"start": v(-423.08, 64.8) * mm, "end": v(-429.43, 64.8) * mm});
            skLineSegment(sketch, "E340", {"start": v(-429.43, 64.8) * mm, "end": v(-429.43, 58.45) * mm});
            skLineSegment(sketch, "E341", {"start": v(-429.43, 58.45) * mm, "end": v(-453.56, 58.45) * mm});
            skLineSegment(sketch, "E342", {"start": v(-453.56, 58.45) * mm, "end": v(-453.56, 71.15) * mm});
            skLineSegment(sketch, "E343", {"start": v(-377.36, -80.05) * mm, "end": v(-377.36, -73.63) * mm});
            skLineSegment(sketch, "E344", {"start": v(-377.36, -73.63) * mm, "end": v(-407.84, -73.63) * mm});
            skLineSegment(sketch, "E345", {"start": v(-407.84, -73.63) * mm, "end": v(-407.84, -55.85) * mm});
            skLineSegment(sketch, "E346", {"start": v(-407.84, -55.85) * mm, "end": v(-401.49, -55.85) * mm});
            skLineSegment(sketch, "E347", {"start": v(-401.49, -55.85) * mm, "end": v(-401.49, -62.2) * mm});
            skLineSegment(sketch, "E348", {"start": v(-401.49, -62.2) * mm, "end": v(-377.36, -62.2) * mm});
            skLineSegment(sketch, "E349", {"start": v(-377.36, -62.2) * mm, "end": v(-377.36, -49.5) * mm});
            skLineSegment(sketch, "E350", {"start": v(-377.36, -49.5) * mm, "end": v(-407.84, -49.5) * mm});
            skLineSegment(sketch, "E351", {"start": v(-407.84, -49.5) * mm, "end": v(-407.84, -31.72) * mm});
            skLineSegment(sketch, "E352", {"start": v(-407.84, -31.72) * mm, "end": v(-401.49, -31.72) * mm});
            skLineSegment(sketch, "E353", {"start": v(-401.49, -31.72) * mm, "end": v(-401.49, -38.07) * mm});
            skLineSegment(sketch, "E354", {"start": v(-401.49, -38.07) * mm, "end": v(-377.36, -38.07) * mm});
            skLineSegment(sketch, "E355", {"start": v(-377.36, -38.07) * mm, "end": v(-377.36, -25.37) * mm});
            skLineSegment(sketch, "E356", {"start": v(-377.36, -25.37) * mm, "end": v(-407.84, -25.37) * mm});
            skLineSegment(sketch, "E357", {"start": v(-407.84, -25.37) * mm, "end": v(-407.84, -7.6) * mm});
            skLineSegment(sketch, "E358", {"start": v(-407.84, -7.6) * mm, "end": v(-401.49, -7.6) * mm});
            skLineSegment(sketch, "E359", {"start": v(-401.49, -7.6) * mm, "end": v(-401.49, -13.94) * mm});
            skLineSegment(sketch, "E360", {"start": v(-401.49, -13.94) * mm, "end": v(-377.36, -13.94) * mm});
            skLineSegment(sketch, "E361", {"start": v(-377.36, -13.94) * mm, "end": v(-377.36, -1.24) * mm});
            skLineSegment(sketch, "E362", {"start": v(-377.36, -1.24) * mm, "end": v(-407.84, -1.24) * mm});
            skLineSegment(sketch, "E363", {"start": v(-407.84, -1.24) * mm, "end": v(-407.84, 16.54) * mm});
            skLineSegment(sketch, "E364", {"start": v(-407.84, 16.54) * mm, "end": v(-401.49, 16.54) * mm});
            skLineSegment(sketch, "E365", {"start": v(-401.49, 16.54) * mm, "end": v(-401.49, 10.19) * mm});
            skLineSegment(sketch, "E366", {"start": v(-401.49, 10.19) * mm, "end": v(-377.36, 10.19) * mm});
            skLineSegment(sketch, "E367", {"start": v(-377.36, 10.19) * mm, "end": v(-377.36, 22.89) * mm});
            skLineSegment(sketch, "E368", {"start": v(-377.36, 22.89) * mm, "end": v(-407.84, 22.89) * mm});
            skLineSegment(sketch, "E369", {"start": v(-407.84, 22.89) * mm, "end": v(-407.84, 40.67) * mm});
            skLineSegment(sketch, "E370", {"start": v(-407.84, 40.67) * mm, "end": v(-401.49, 40.67) * mm});
            skLineSegment(sketch, "E371", {"start": v(-401.49, 40.67) * mm, "end": v(-401.49, 34.32) * mm});
            skLineSegment(sketch, "E372", {"start": v(-401.49, 34.32) * mm, "end": v(-377.36, 34.32) * mm});
            skLineSegment(sketch, "E373", {"start": v(-377.36, 34.32) * mm, "end": v(-377.36, 47.02) * mm});
            skLineSegment(sketch, "E374", {"start": v(-377.36, 47.02) * mm, "end": v(-407.84, 47.02) * mm});
            skLineSegment(sketch, "E375", {"start": v(-407.84, 47.02) * mm, "end": v(-407.84, 64.8) * mm});
            skLineSegment(sketch, "E376", {"start": v(-407.84, 64.8) * mm, "end": v(-401.49, 64.8) * mm});
            skLineSegment(sketch, "E377", {"start": v(-401.49, 64.8) * mm, "end": v(-401.49, 58.45) * mm});
            skLineSegment(sketch, "E378", {"start": v(-401.49, 58.45) * mm, "end": v(-377.36, 58.45) * mm});
            skLineSegment(sketch, "E379", {"start": v(-377.36, 58.45) * mm, "end": v(-377.36, 71.15) * mm});
            skLineSegment(sketch, "E380", {"start": v(-423.08, 47.02) * mm, "end": v(-423.08, 64.8) * mm});
            skLineSegment(sketch, "E381", {"start": v(-423.08, -73.63) * mm, "end": v(-423.08, -55.85) * mm});
            skLineSegment(sketch, "E382", {"start": v(-429.43, -62.2) * mm, "end": v(-429.43, -55.85) * mm});
            skLineSegment(sketch, "E383", {"start": v(-429.43, -55.85) * mm, "end": v(-423.08, -55.85) * mm});
            skLineSegment(sketch, "E384", {"start": v(-423.08, -73.63) * mm, "end": v(-453.56, -73.63) * mm});
            skLineSegment(sketch, "E385", {"start": v(-453.56, -62.2) * mm, "end": v(-453.56, -49.5) * mm});
            skLineSegment(sketch, "E386", {"start": v(-453.56, -73.63) * mm, "end": v(-453.56, -80.05) * mm});
            skLineSegment(sketch, "E387", {"start": v(-453.56, -62.2) * mm, "end": v(-429.43, -62.2) * mm});
            skLineSegment(sketch, "E388", {"start": v(-453.56, -80.05) * mm, "end": v(-377.36, -80.05) * mm});
            skLineSegment(sketch, "E389", {"start": v(-453.56, 71.15) * mm, "end": v(-377.36, 71.15) * mm});
            skPoint(sketch, "E390", {"position": v(-415.46, 71.15) * mm});
            skPoint(sketch, "E391", {"position": v(-415.46, -80.05) * mm});
            skLineSegment(sketch, "E392", {"start": v(-542.46, -49.5) * mm, "end": v(-511.98, -49.5) * mm});
            skLineSegment(sketch, "E393", {"start": v(-511.98, -49.5) * mm, "end": v(-511.98, -31.72) * mm});
            skLineSegment(sketch, "E394", {"start": v(-511.98, -31.72) * mm, "end": v(-518.33, -31.72) * mm});
            skLineSegment(sketch, "E395", {"start": v(-518.33, -31.72) * mm, "end": v(-518.33, -38.07) * mm});
            skLineSegment(sketch, "E396", {"start": v(-518.33, -38.07) * mm, "end": v(-542.46, -38.07) * mm});
            skLineSegment(sketch, "E397", {"start": v(-542.46, -38.07) * mm, "end": v(-542.46, -25.37) * mm});
            skLineSegment(sketch, "E398", {"start": v(-542.46, -25.37) * mm, "end": v(-511.98, -25.37) * mm});
            skLineSegment(sketch, "E399", {"start": v(-511.98, -25.37) * mm, "end": v(-511.98, -7.6) * mm});
            skLineSegment(sketch, "E400", {"start": v(-511.98, -7.6) * mm, "end": v(-518.33, -7.6) * mm});
            skLineSegment(sketch, "E401", {"start": v(-518.33, -7.6) * mm, "end": v(-518.33, -13.94) * mm});
            skLineSegment(sketch, "E402", {"start": v(-518.33, -13.94) * mm, "end": v(-542.46, -13.94) * mm});
            skLineSegment(sketch, "E403", {"start": v(-542.46, -13.94) * mm, "end": v(-542.46, -1.24) * mm});
            skLineSegment(sketch, "E404", {"start": v(-542.46, -1.24) * mm, "end": v(-511.98, -1.24) * mm});
            skLineSegment(sketch, "E405", {"start": v(-511.98, -1.24) * mm, "end": v(-511.98, 16.54) * mm});
            skLineSegment(sketch, "E406", {"start": v(-511.98, 16.54) * mm, "end": v(-518.33, 16.54) * mm});
            skLineSegment(sketch, "E407", {"start": v(-518.33, 16.54) * mm, "end": v(-518.33, 10.19) * mm});
            skLineSegment(sketch, "E408", {"start": v(-518.33, 10.19) * mm, "end": v(-542.46, 10.19) * mm});
            skLineSegment(sketch, "E409", {"start": v(-542.46, 10.19) * mm, "end": v(-542.46, 22.89) * mm});
            skLineSegment(sketch, "E410", {"start": v(-542.46, 22.89) * mm, "end": v(-511.98, 22.89) * mm});
            skLineSegment(sketch, "E411", {"start": v(-511.98, 22.89) * mm, "end": v(-511.98, 40.67) * mm});
            skLineSegment(sketch, "E412", {"start": v(-511.98, 40.67) * mm, "end": v(-518.33, 40.67) * mm});
            skLineSegment(sketch, "E413", {"start": v(-518.33, 40.67) * mm, "end": v(-518.33, 34.32) * mm});
            skLineSegment(sketch, "E414", {"start": v(-518.33, 34.32) * mm, "end": v(-542.46, 34.32) * mm});
            skLineSegment(sketch, "E415", {"start": v(-542.46, 34.32) * mm, "end": v(-542.46, 47.02) * mm});
            skLineSegment(sketch, "E416", {"start": v(-542.46, 47.02) * mm, "end": v(-511.98, 47.02) * mm});
            skLineSegment(sketch, "E417", {"start": v(-511.98, 64.8) * mm, "end": v(-518.33, 64.8) * mm});
            skLineSegment(sketch, "E418", {"start": v(-518.33, 64.8) * mm, "end": v(-518.33, 58.45) * mm});
            skLineSegment(sketch, "E419", {"start": v(-518.33, 58.45) * mm, "end": v(-542.46, 58.45) * mm});
            skLineSegment(sketch, "E420", {"start": v(-542.46, 58.45) * mm, "end": v(-542.46, 71.15) * mm});
            skLineSegment(sketch, "E421", {"start": v(-466.26, -80.05) * mm, "end": v(-466.26, -73.63) * mm});
            skLineSegment(sketch, "E422", {"start": v(-466.26, -73.63) * mm, "end": v(-496.74, -73.63) * mm});
            skLineSegment(sketch, "E423", {"start": v(-496.74, -73.63) * mm, "end": v(-496.74, -55.85) * mm});
            skLineSegment(sketch, "E424", {"start": v(-496.74, -55.85) * mm, "end": v(-490.39, -55.85) * mm});
            skLineSegment(sketch, "E425", {"start": v(-490.39, -55.85) * mm, "end": v(-490.39, -62.2) * mm});
            skLineSegment(sketch, "E426", {"start": v(-490.39, -62.2) * mm, "end": v(-466.26, -62.2) * mm});
            skLineSegment(sketch, "E427", {"start": v(-466.26, -62.2) * mm, "end": v(-466.26, -49.5) * mm});
            skLineSegment(sketch, "E428", {"start": v(-466.26, -49.5) * mm, "end": v(-496.74, -49.5) * mm});
            skLineSegment(sketch, "E429", {"start": v(-496.74, -49.5) * mm, "end": v(-496.74, -31.72) * mm});
            skLineSegment(sketch, "E430", {"start": v(-496.74, -31.72) * mm, "end": v(-490.39, -31.72) * mm});
            skLineSegment(sketch, "E431", {"start": v(-490.39, -31.72) * mm, "end": v(-490.39, -38.07) * mm});
            skLineSegment(sketch, "E432", {"start": v(-490.39, -38.07) * mm, "end": v(-466.26, -38.07) * mm});
            skLineSegment(sketch, "E433", {"start": v(-466.26, -38.07) * mm, "end": v(-466.26, -25.37) * mm});
            skLineSegment(sketch, "E434", {"start": v(-466.26, -25.37) * mm, "end": v(-496.74, -25.37) * mm});
            skLineSegment(sketch, "E435", {"start": v(-496.74, -25.37) * mm, "end": v(-496.74, -7.6) * mm});
            skLineSegment(sketch, "E436", {"start": v(-496.74, -7.6) * mm, "end": v(-490.39, -7.6) * mm});
            skLineSegment(sketch, "E437", {"start": v(-490.39, -7.6) * mm, "end": v(-490.39, -13.94) * mm});
            skLineSegment(sketch, "E438", {"start": v(-490.39, -13.94) * mm, "end": v(-466.26, -13.94) * mm});
            skLineSegment(sketch, "E439", {"start": v(-466.26, -13.94) * mm, "end": v(-466.26, -1.24) * mm});
            skLineSegment(sketch, "E440", {"start": v(-466.26, -1.24) * mm, "end": v(-496.74, -1.24) * mm});
            skLineSegment(sketch, "E441", {"start": v(-496.74, -1.24) * mm, "end": v(-496.74, 16.54) * mm});
            skLineSegment(sketch, "E442", {"start": v(-496.74, 16.54) * mm, "end": v(-490.39, 16.54) * mm});
            skLineSegment(sketch, "E443", {"start": v(-490.39, 16.54) * mm, "end": v(-490.39, 10.19) * mm});
            skLineSegment(sketch, "E444", {"start": v(-490.39, 10.19) * mm, "end": v(-466.26, 10.19) * mm});
            skLineSegment(sketch, "E445", {"start": v(-466.26, 10.19) * mm, "end": v(-466.26, 22.89) * mm});
            skLineSegment(sketch, "E446", {"start": v(-466.26, 22.89) * mm, "end": v(-496.74, 22.89) * mm});
            skLineSegment(sketch, "E447", {"start": v(-496.74, 22.89) * mm, "end": v(-496.74, 40.67) * mm});
            skLineSegment(sketch, "E448", {"start": v(-496.74, 40.67) * mm, "end": v(-490.39, 40.67) * mm});
            skLineSegment(sketch, "E449", {"start": v(-490.39, 40.67) * mm, "end": v(-490.39, 34.32) * mm});
            skLineSegment(sketch, "E450", {"start": v(-490.39, 34.32) * mm, "end": v(-466.26, 34.32) * mm});
            skLineSegment(sketch, "E451", {"start": v(-466.26, 34.32) * mm, "end": v(-466.26, 47.02) * mm});
            skLineSegment(sketch, "E452", {"start": v(-466.26, 47.02) * mm, "end": v(-496.74, 47.02) * mm});
            skLineSegment(sketch, "E453", {"start": v(-496.74, 47.02) * mm, "end": v(-496.74, 64.8) * mm});
            skLineSegment(sketch, "E454", {"start": v(-496.74, 64.8) * mm, "end": v(-490.39, 64.8) * mm});
            skLineSegment(sketch, "E455", {"start": v(-490.39, 64.8) * mm, "end": v(-490.39, 58.45) * mm});
            skLineSegment(sketch, "E456", {"start": v(-490.39, 58.45) * mm, "end": v(-466.26, 58.45) * mm});
            skLineSegment(sketch, "E457", {"start": v(-466.26, 58.45) * mm, "end": v(-466.26, 71.15) * mm});
            skLineSegment(sketch, "E458", {"start": v(-511.98, 47.02) * mm, "end": v(-511.98, 64.8) * mm});
            skLineSegment(sketch, "E459", {"start": v(-511.98, -73.63) * mm, "end": v(-511.98, -55.85) * mm});
            skLineSegment(sketch, "E460", {"start": v(-518.33, -62.2) * mm, "end": v(-518.33, -55.85) * mm});
            skLineSegment(sketch, "E461", {"start": v(-518.33, -55.85) * mm, "end": v(-511.98, -55.85) * mm});
            skLineSegment(sketch, "E462", {"start": v(-511.98, -73.63) * mm, "end": v(-542.46, -73.63) * mm});
            skLineSegment(sketch, "E463", {"start": v(-542.46, -62.2) * mm, "end": v(-542.46, -49.5) * mm});
            skLineSegment(sketch, "E464", {"start": v(-542.46, -73.63) * mm, "end": v(-542.46, -80.05) * mm});
            skLineSegment(sketch, "E465", {"start": v(-542.46, -62.2) * mm, "end": v(-518.33, -62.2) * mm});
            skLineSegment(sketch, "E466", {"start": v(-542.46, -80.05) * mm, "end": v(-466.26, -80.05) * mm});
            skLineSegment(sketch, "E467", {"start": v(-542.46, 71.15) * mm, "end": v(-466.26, 71.15) * mm});
            skPoint(sketch, "E468", {"position": v(-504.36, 71.15) * mm});
            skPoint(sketch, "E469", {"position": v(-504.36, -80.05) * mm});
            skLineSegment(sketch, "E470", {"start": v(-288.46, 71.15) * mm, "end": v(-275.76, 71.15) * mm});
            skPoint(sketch, "E471", {"position": v(-282.1, 71.15) * mm});
            skSolve(sketch);
        }
        {
            var Q0;
            Q0=makeQuery(id+"F0.imprint","IMPRINT",FACE,{"disambiguationData":[TD([[makeQuery(id+"F0.imprint","IMPRINT",EDGE,{"derivedFrom":sQuery(id+"F0.wireOp",EDGE,"E0")}),1.0]])]});
            extrude(context, id + "F1", {"entities" : qUnion([Q0]), "depth" : 6.35 * mm});
        }
    });
